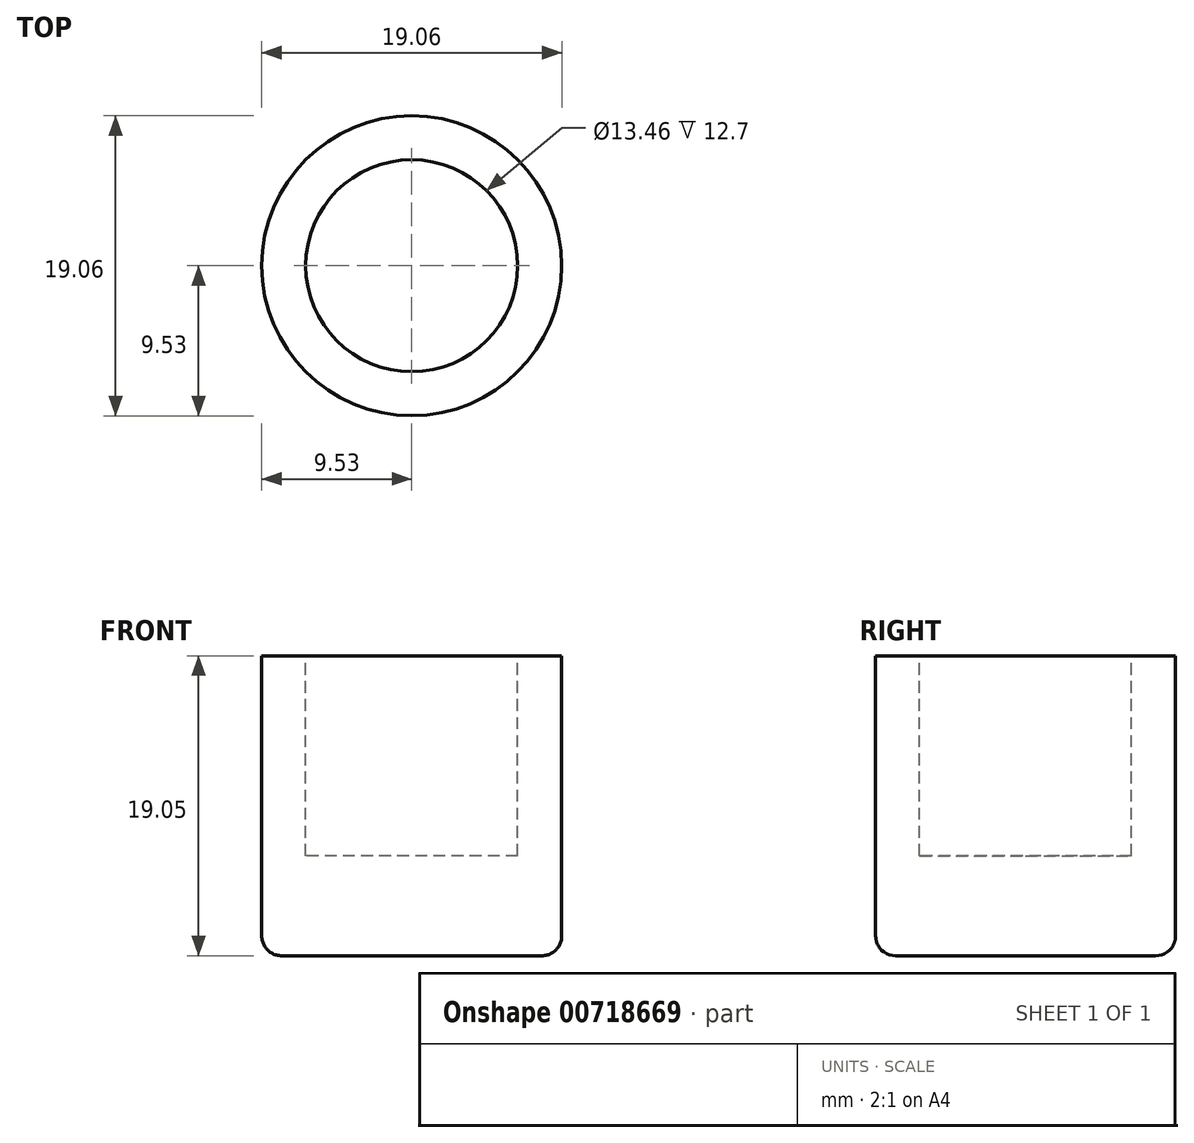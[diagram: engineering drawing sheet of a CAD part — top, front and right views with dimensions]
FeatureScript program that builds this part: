
annotation { "Feature Type Name" : "Feature", "Feature Type Description" : "" }
export const myFeature = defineFeature(function(context is Context, id is Id, definition is map)
    precondition{}
    {
        {
            var Q0;
            Q0=qCreatedBy(makeId("Top.planeOp"),FACE);
            var sketch = newSketch(context, id + "F0", { "sketchPlane" : qUnion([Q0])});
            skCircle(sketch, "E0", {"center": v(0, 0) * mm, "radius": 9.53 * mm});
            skSolve(sketch);
        }
        {
            var Q0;
            Q0=makeQuery(id+"F0.imprint","IMPRINT",FACE,{"disambiguationData":[TD([[makeQuery(id+"F0.imprint","IMPRINT",EDGE,{"derivedFrom":sQuery(id+"F0.wireOp",EDGE,"E0")}),1.0]])]});
            extrude(context, id + "F1", {"entities" : qUnion([Q0]), "depth" : 19.05 * mm, "offsetDistance" : 25.4 * mm});
        }
        {
            var Q0;
            Q0=makeQuery(id+"F1.opExtrude","CAP_FACE",FACE,{"disambiguationData":[OSD([sQuery(id+"F0.wireOp",EDGE,"E0")])],"isStart":false});
            var sketch = newSketch(context, id + "F2", { "sketchPlane" : qUnion([Q0])});
            skCircle(sketch, "E1", {"center": v(0, 0) * mm, "radius": 6.73 * mm});
            skSolve(sketch);
        }
        {
            var Q0;
            Q0=makeQuery(id+"F2.imprint","IMPRINT",FACE,{"disambiguationData":[TD([[makeQuery(id+"F2.imprint","IMPRINT",EDGE,{"derivedFrom":sQuery(id+"F2.wireOp",EDGE,"E1")}),1.0]])]});
            extrude(context, id + "F3", {"entities" : qUnion([Q0]), "operationType" : NewBodyOperationType.REMOVE, "oppositeDirection" : true, "depth" : 12.7 * mm, "offsetDistance" : 25.4 * mm});
        }
        {
            var Q0;
            Q0=makeQuery(id+"F1.opExtrude","CAP_EDGE",EDGE,{"disambiguationData":[OSD([sQuery(id+"F0.wireOp",EDGE,"E0")])],"isStart":true});
            fillet(context, id + "F4", {"entities" : qUnion([Q0]), "radius" : 1.27 * mm, "tangentPropagation" : true, "allowEdgeOverflow" : false});
        }
    });
